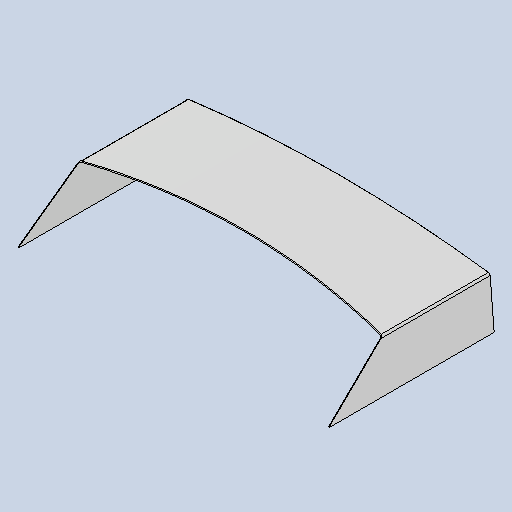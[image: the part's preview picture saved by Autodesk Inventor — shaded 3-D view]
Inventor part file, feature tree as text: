
AUTODESK INVENTOR PART (.ipt)
format: ipt  version: 2025 (Build 290162010, 162A)  size: 307,200 bytes
history: native  units: mm
features: other x4, sheet_metal_op x3, sketch x3, mirror x1, extrude x1, fillet x1
ambient origin geometry x8: Origin, YZ Plane, XZ Plane, XY Plane, X Axis, Y Axis, Z Axis, Center Point
bodies: Body1 (feature_tree)
feature tree (13):
  sheet_metal_op  "Contour Flange2"
  mirror  "Mirror2"
  extrude  "Extrusion2"  Depth=3.0mm
  fillet  "Fillet1"  Radius=1.5mm
  other  "Mark2"
  other  "A-Side Definition"
  sketch  "Sketch1"  dims[d36=3.0mm d37=3.0mm d38=1.5mm]
  other  "Plate2"
  sheet_metal_op  "Bend2"
  sheet_metal_op  "Corner2"
  sketch  "Sketch2"  dims[d39=6.0mm]
  sketch  "Sketch4"  dims[d40=3.0mm d41=819.0mm d42=3.0mm d43=3.0mm d44=12.0mm d45=3.0mm d46=3.0mm d65=6.0mm d78=3.0mm d80=3.0mm d123=0.0mm d124=0.0mm d128=2.0mm d134=1500.0mm d135=2700.0mm d136=2100.0mm d137=8.0mm d138=50.0mm d139=50.0mm d140=3.0mm d141=10.0mm d142=241.9mm d146=3.0mm d148=5.0mm d149=6.981317mm d150=500.0mm]
  other  "Definition1"
